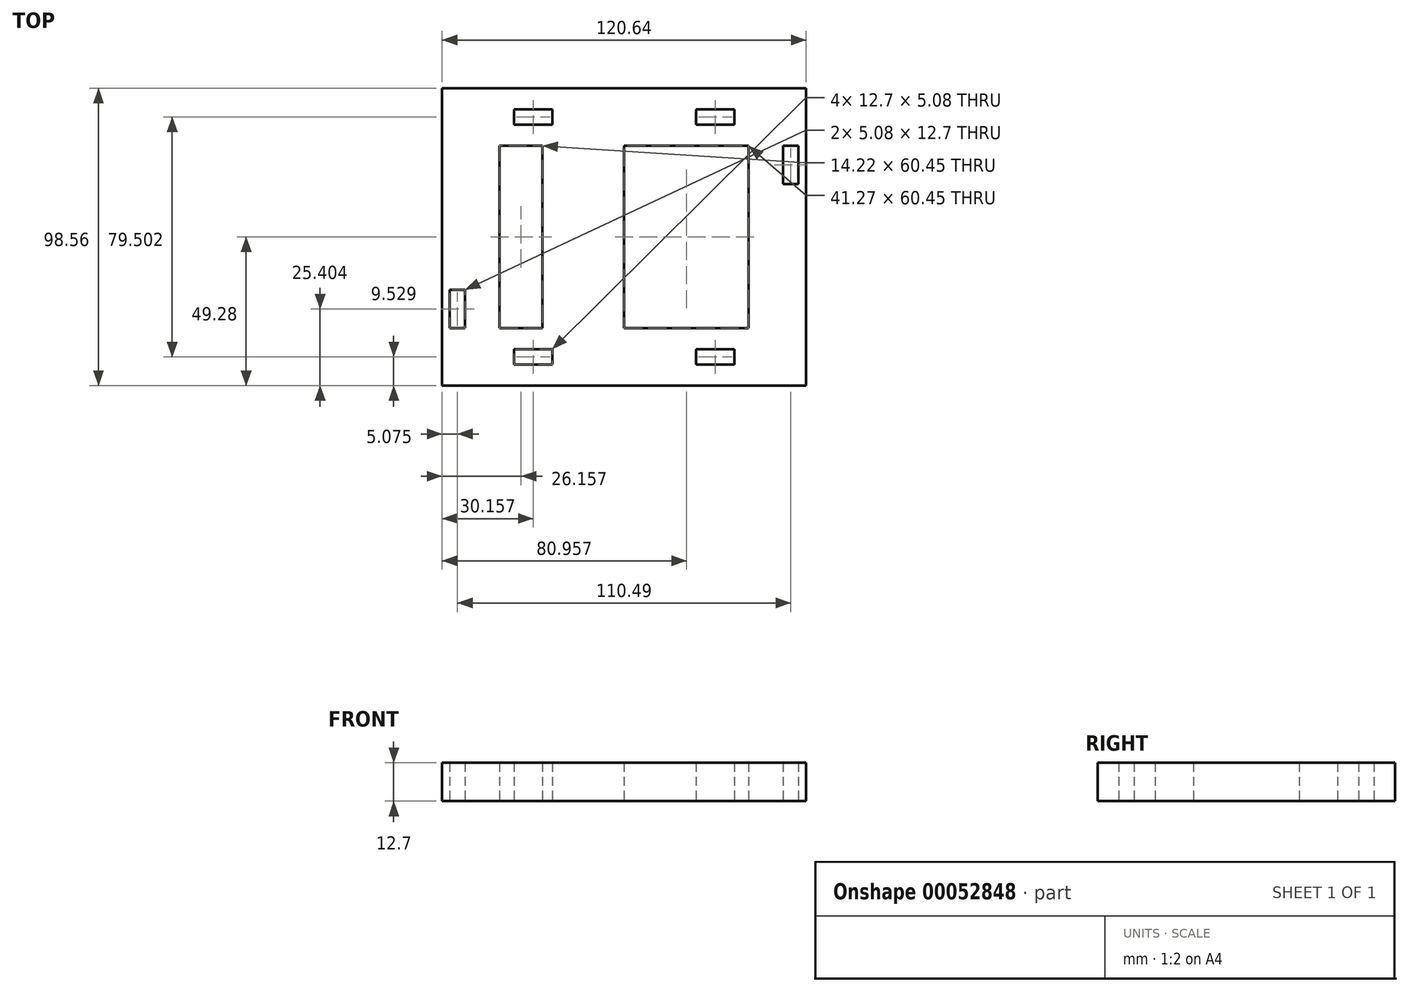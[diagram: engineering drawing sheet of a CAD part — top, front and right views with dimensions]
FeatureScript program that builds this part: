
annotation { "Feature Type Name" : "Feature", "Feature Type Description" : "" }
export const myFeature = defineFeature(function(context is Context, id is Id, definition is map)
    precondition{}
    {
        {
            var Q0;
            Q0=qCreatedBy(makeId("Top.planeOp"),FACE);
            var sketch = newSketch(context, id + "F0", { "sketchPlane" : qUnion([Q0])});
            skLineSegment(sketch, "E0.rect.bottom", {"start": v(27.05, -30.23) * mm, "end": v(-27.05, -30.23) * mm});
            skLineSegment(sketch, "E0.rect.top", {"start": v(27.05, 30.23) * mm, "end": v(-27.05, 30.23) * mm});
            skLineSegment(sketch, "E0.rect.left", {"start": v(27.05, -30.23) * mm, "end": v(27.05, 30.23) * mm});
            skLineSegment(sketch, "E0.rect.right", {"start": v(-27.05, -30.23) * mm, "end": v(-27.05, 30.23) * mm});
            skPoint(sketch, "E0.rect.middle", {"position": v(0, 0) * mm});
            skLineSegment(sketch, "E1.bottom", {"start": v(-27.05, -30.23) * mm, "end": v(-41.28, -30.23) * mm});
            skLineSegment(sketch, "E1.top", {"start": v(-27.05, 30.23) * mm, "end": v(-41.28, 30.23) * mm});
            skLineSegment(sketch, "E1.right", {"start": v(-41.28, -30.23) * mm, "end": v(-41.28, 30.23) * mm});
            skLineSegment(sketch, "E2.bottom", {"start": v(27.05, 30.23) * mm, "end": v(41.27, 30.23) * mm});
            skLineSegment(sketch, "E2.top", {"start": v(27.05, -30.23) * mm, "end": v(41.27, -30.23) * mm});
            skLineSegment(sketch, "E2.left", {"start": v(27.05, 30.23) * mm, "end": v(27.05, -30.23) * mm});
            skLineSegment(sketch, "E2.right", {"start": v(41.27, 30.23) * mm, "end": v(41.27, -30.23) * mm});
            skLineSegment(sketch, "E3.0", {"start": v(27.05, -49.28) * mm, "end": v(-27.05, -49.28) * mm});
            skLineSegment(sketch, "E3.1", {"start": v(27.05, -49.28) * mm, "end": v(60.32, -49.28) * mm});
            skLineSegment(sketch, "E3.2", {"start": v(-27.05, -49.28) * mm, "end": v(-60.32, -49.28) * mm});
            skLineSegment(sketch, "E3.3", {"start": v(60.32, 49.28) * mm, "end": v(60.32, -49.28) * mm});
            skLineSegment(sketch, "E3.4", {"start": v(-60.32, -49.28) * mm, "end": v(-60.33, 49.28) * mm});
            skLineSegment(sketch, "E3.5", {"start": v(-27.05, 49.28) * mm, "end": v(-60.33, 49.28) * mm});
            skLineSegment(sketch, "E3.6", {"start": v(27.05, 49.28) * mm, "end": v(-27.05, 49.28) * mm});
            skLineSegment(sketch, "E3.7", {"start": v(27.05, 49.28) * mm, "end": v(60.32, 49.28) * mm});
            skLineSegment(sketch, "E4", {"start": v(0, -30.23) * mm, "end": v(0, 30.23) * mm});
            skLineSegment(sketch, "E5", {"start": v(0, 30.23) * mm, "end": v(0, 49.28) * mm});
            skLineSegment(sketch, "E6.rect.left", {"start": v(60.32, -39.75) * mm, "end": v(60.32, -39.75) * mm});
            skLineSegment(sketch, "E6.rect.right", {"start": v(-60.32, -39.75) * mm, "end": v(-60.32, -39.75) * mm});
            skPoint(sketch, "E6.rect.middle", {"position": v(0, -39.75) * mm});
            skLineSegment(sketch, "E7", {"start": v(0, 39.75) * mm, "end": v(-60.33, 39.75) * mm});
            skLineSegment(sketch, "E8", {"start": v(0, 39.75) * mm, "end": v(60.32, 39.75) * mm});
            skLineSegment(sketch, "E9.rect.bottom", {"start": v(-36.51, 37.21) * mm, "end": v(-23.81, 37.21) * mm});
            skLineSegment(sketch, "E9.rect.top", {"start": v(-36.51, 42.3) * mm, "end": v(-23.81, 42.3) * mm});
            skLineSegment(sketch, "E9.rect.left", {"start": v(-36.51, 37.21) * mm, "end": v(-36.51, 42.3) * mm});
            skLineSegment(sketch, "E9.rect.right", {"start": v(-23.81, 37.21) * mm, "end": v(-23.81, 42.3) * mm});
            skPoint(sketch, "E9.rect.middle", {"position": v(-30.16, 39.75) * mm});
            skLineSegment(sketch, "E10.rect.bottom", {"start": v(23.81, 37.21) * mm, "end": v(36.51, 37.21) * mm});
            skLineSegment(sketch, "E10.rect.top", {"start": v(23.81, 42.3) * mm, "end": v(36.51, 42.3) * mm});
            skLineSegment(sketch, "E10.rect.left", {"start": v(23.81, 37.21) * mm, "end": v(23.81, 42.3) * mm});
            skLineSegment(sketch, "E10.rect.right", {"start": v(36.51, 37.21) * mm, "end": v(36.51, 42.3) * mm});
            skPoint(sketch, "E10.rect.middle", {"position": v(30.16, 39.75) * mm});
            skLineSegment(sketch, "E11", {"start": v(-30.16, 39.75) * mm, "end": v(-30.16, 30.23) * mm});
            skPoint(sketch, "E11.endSnap0", {"position": v(-30.16, 37.21) * mm});
            skLineSegment(sketch, "E12", {"start": v(30.16, 39.75) * mm, "end": v(30.16, 30.23) * mm});
            skLineSegment(sketch, "E13.trimOffspring", {"start": v(-30.16, -30.23) * mm, "end": v(-30.16, -49.28) * mm});
            skLineSegment(sketch, "E14.rect.bottom", {"start": v(23.81, -42.3) * mm, "end": v(36.51, -42.3) * mm});
            skLineSegment(sketch, "E14.rect.top", {"start": v(23.81, -37.21) * mm, "end": v(36.51, -37.21) * mm});
            skPoint(sketch, "E14.rect.middle", {"position": v(30.16, -39.75) * mm});
            skLineSegment(sketch, "E15.rect.bottom", {"start": v(-23.81, -42.3) * mm, "end": v(-36.51, -42.3) * mm});
            skLineSegment(sketch, "E15.rect.top", {"start": v(-23.81, -37.21) * mm, "end": v(-36.51, -37.21) * mm});
            skLineSegment(sketch, "E15.rect.left", {"start": v(-23.81, -42.3) * mm, "end": v(-23.81, -37.21) * mm});
            skLineSegment(sketch, "E15.rect.right", {"start": v(-36.51, -42.3) * mm, "end": v(-36.51, -37.21) * mm});
            skPoint(sketch, "E15.rect.middle", {"position": v(-30.16, -39.75) * mm});
            skLineSegment(sketch, "E16", {"start": v(23.81, -42.3) * mm, "end": v(23.81, -37.21) * mm});
            skLineSegment(sketch, "E17", {"start": v(36.51, -42.3) * mm, "end": v(36.51, -37.21) * mm});
            skPoint(sketch, "E18", {"position": v(-60.32, -30.23) * mm});
            skPoint(sketch, "E19", {"position": v(-60.33, -17.53) * mm});
            skLineSegment(sketch, "E20", {"start": v(-60.32, -30.23) * mm, "end": v(-57.78, -30.23) * mm});
            skLineSegment(sketch, "E21", {"start": v(-57.78, -30.23) * mm, "end": v(-57.78, -17.53) * mm});
            skLineSegment(sketch, "E22", {"start": v(-57.78, -17.53) * mm, "end": v(-60.33, -17.53) * mm});
            skLineSegment(sketch, "E23", {"start": v(-57.78, -30.23) * mm, "end": v(-52.7, -30.23) * mm});
            skLineSegment(sketch, "E24", {"start": v(-52.7, -30.23) * mm, "end": v(-52.7, -17.53) * mm});
            skLineSegment(sketch, "E25", {"start": v(-52.7, -17.53) * mm, "end": v(-57.78, -17.53) * mm});
            skPoint(sketch, "E26", {"position": v(60.32, 30.23) * mm});
            skPoint(sketch, "E27", {"position": v(60.32, 17.53) * mm});
            skLineSegment(sketch, "E28", {"start": v(60.32, 30.23) * mm, "end": v(57.79, 30.23) * mm});
            skLineSegment(sketch, "E29", {"start": v(57.79, 30.23) * mm, "end": v(57.79, 17.53) * mm});
            skLineSegment(sketch, "E30", {"start": v(57.79, 17.53) * mm, "end": v(60.32, 17.53) * mm});
            skLineSegment(sketch, "E31", {"start": v(57.79, 30.23) * mm, "end": v(52.7, 30.23) * mm});
            skLineSegment(sketch, "E32", {"start": v(52.7, 30.23) * mm, "end": v(52.7, 17.53) * mm});
            skLineSegment(sketch, "E33", {"start": v(52.7, 17.53) * mm, "end": v(57.79, 17.53) * mm});
            skSolve(sketch);
        }
        {
            var Q0;
            {var subQ5=sQuery(id+"F0.wireOp",EDGE,"E3.5");Q0=makeQuery(id+"F0.imprint","IMPRINT",FACE,{"disambiguationData":[TD([[makeQuery(id+"F0.imprint","IMPRINT",EDGE,{"derivedFrom":subQ5}),1.0]])]});}
            var Q1;
            {var subQ20=sQuery(id+"F0.wireOp",EDGE,"E1.right");Q1=makeQuery(id+"F0.imprint","IMPRINT",FACE,{"disambiguationData":[TD([[makeQuery(id+"F0.imprint","IMPRINT",EDGE,{"derivedFrom":subQ20}),1.0]])]});}
            var Q2;
            {var subQ20=sQuery(id+"F0.wireOp",EDGE,"E1.right");Q2=makeQuery(id+"F0.imprint","IMPRINT",FACE,{"disambiguationData":[TD([[makeQuery(id+"F0.imprint","IMPRINT",EDGE,{"derivedFrom":subQ20}),1.0]])]});}
            var Q3;
            {var subQ7=sQuery(id+"F0.wireOp",EDGE,"E9.rect.right");var subQ8=sQuery(id+"F0.wireOp",EDGE,"E9.rect.bottom");var subQ9=makeQuery(id+"F0.imprint","INTERSECT",VERTEX,{"derivedFrom":[subQ8,subQ7]});Q3=makeQuery(id+"F0.imprint","IMPRINT",FACE,{"disambiguationData":[TD([[makeQuery(id+"F0.imprint","IMPRINT",EDGE,{"disambiguationData":[TD([[subQ9,1.0]])],"derivedFrom":subQ8}),-1.0]])]});}
            var Q4;
            {var subQ0=sQuery(id+"F0.wireOp",EDGE,"E0.rect.right");Q4=makeQuery(id+"F0.imprint","IMPRINT",FACE,{"disambiguationData":[TD([[makeQuery(id+"F0.imprint","IMPRINT",EDGE,{"derivedFrom":subQ0}),-1.0]])]});}
            var Q5;
            {var subQ0=sQuery(id+"F0.wireOp",EDGE,"E2.left");Q5=makeQuery(id+"F0.imprint","IMPRINT",FACE,{"disambiguationData":[TD([[makeQuery(id+"F0.imprint","IMPRINT",EDGE,{"derivedFrom":subQ0}),-1.0]])]});}
            var Q6;
            {var subQ21=sQuery(id+"F0.wireOp",EDGE,"E2.right");Q6=makeQuery(id+"F0.imprint","IMPRINT",FACE,{"disambiguationData":[TD([[makeQuery(id+"F0.imprint","IMPRINT",EDGE,{"derivedFrom":subQ21}),1.0]])]});}
            var Q7;
            {var subQ21=sQuery(id+"F0.wireOp",EDGE,"E2.right");Q7=makeQuery(id+"F0.imprint","IMPRINT",FACE,{"disambiguationData":[TD([[makeQuery(id+"F0.imprint","IMPRINT",EDGE,{"derivedFrom":subQ21}),1.0]])]});}
            var Q8;
            {var subQ3=sQuery(id+"F0.wireOp",EDGE,"E10.rect.left");var subQ11=sQuery(id+"F0.wireOp",EDGE,"E10.rect.bottom");var subQ12=makeQuery(id+"F0.imprint","INTERSECT",VERTEX,{"derivedFrom":[subQ11,subQ3]});Q8=makeQuery(id+"F0.imprint","IMPRINT",FACE,{"disambiguationData":[TD([[makeQuery(id+"F0.imprint","IMPRINT",EDGE,{"disambiguationData":[TD([[subQ12,-1.0]])],"derivedFrom":subQ11}),-1.0]])]});}
            var Q9;
            {var subQ5=sQuery(id+"F0.wireOp",EDGE,"E3.7");Q9=makeQuery(id+"F0.imprint","IMPRINT",FACE,{"disambiguationData":[TD([[makeQuery(id+"F0.imprint","IMPRINT",EDGE,{"derivedFrom":subQ5}),-1.0]])]});}
            var Q10;
            {var subQ10=sQuery(id+"F0.wireOp",EDGE,"E3.0");Q10=makeQuery(id+"F0.imprint","IMPRINT",FACE,{"disambiguationData":[TD([[makeQuery(id+"F0.imprint","IMPRINT",EDGE,{"derivedFrom":subQ10}),-1.0]])]});}
            var Q11;
            {var subQ0=sQuery(id+"F0.wireOp",EDGE,"E28");Q11=makeQuery(id+"F0.imprint","IMPRINT",FACE,{"disambiguationData":[TD([[makeQuery(id+"F0.imprint","IMPRINT",EDGE,{"derivedFrom":subQ0}),1.0]])]});}
            var Q12;
            {var subQ0=sQuery(id+"F0.wireOp",EDGE,"E20");Q12=makeQuery(id+"F0.imprint","IMPRINT",FACE,{"disambiguationData":[TD([[makeQuery(id+"F0.imprint","IMPRINT",EDGE,{"derivedFrom":subQ0}),1.0]])]});}
            extrude(context, id + "F1", {"entities" : qUnion([Q0, Q1, Q2, Q3, Q4, Q5, Q6, Q7, Q8, Q9, Q10, Q11, Q12]), "depth" : 12.7 * mm});
        }
    });
